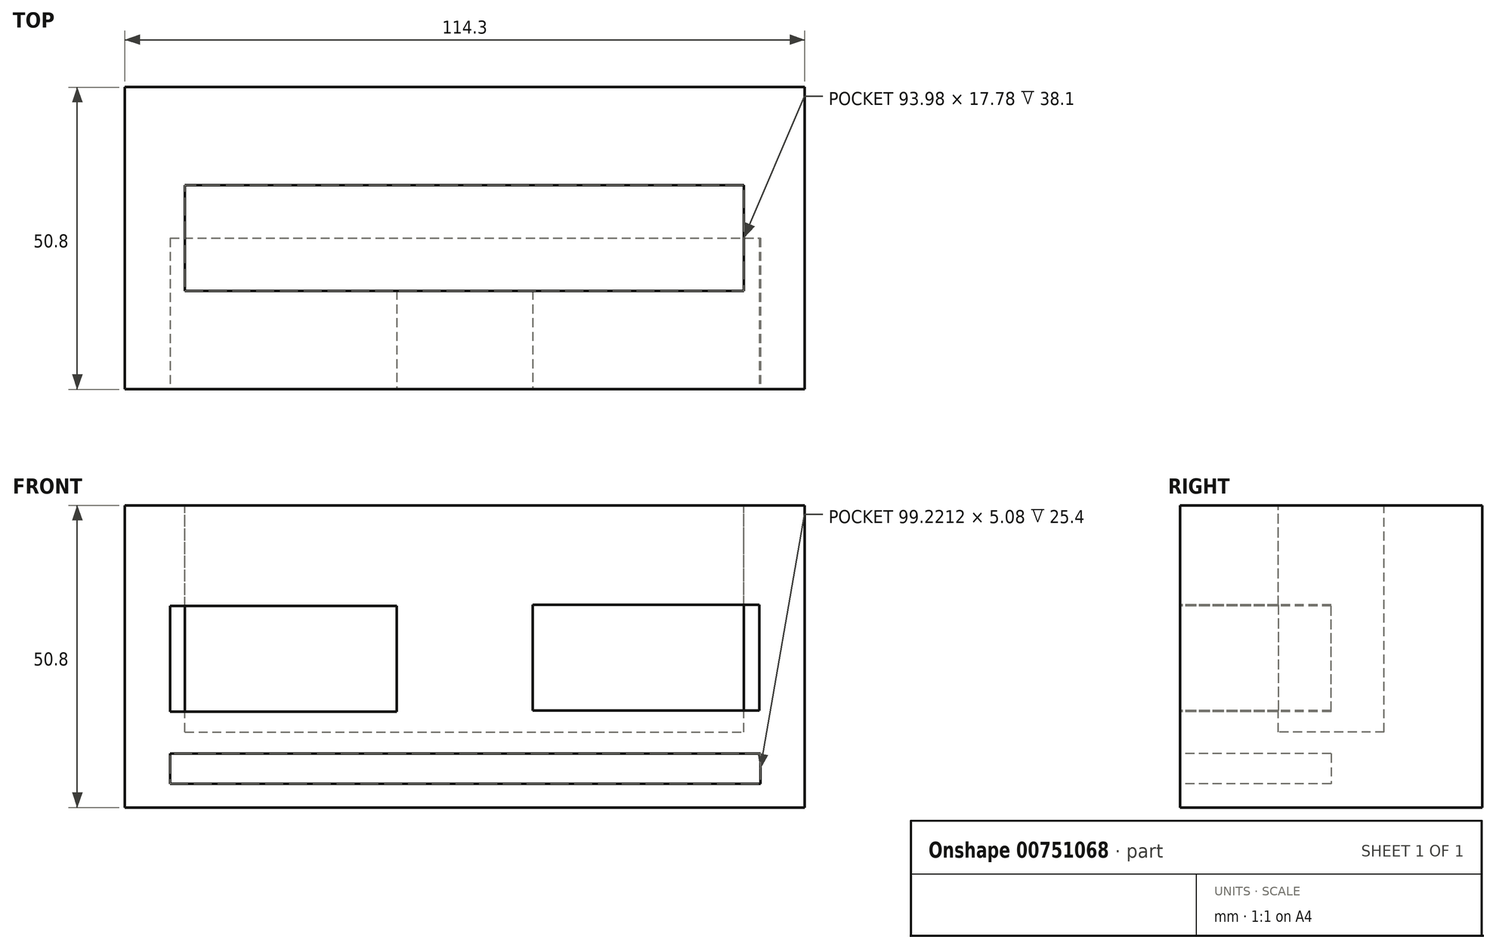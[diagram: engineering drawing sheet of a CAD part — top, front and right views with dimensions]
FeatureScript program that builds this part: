
annotation { "Feature Type Name" : "Feature", "Feature Type Description" : "" }
export const myFeature = defineFeature(function(context is Context, id is Id, definition is map)
    precondition{}
    {
        {
            var Q0;
            Q0=qCreatedBy(makeId("Top.planeOp"),FACE);
            var sketch = newSketch(context, id + "F0", { "sketchPlane" : qUnion([Q0])});
            skLineSegment(sketch, "E0.bottom", {"start": v(-58.02, 2.67) * mm, "end": v(56.28, 2.67) * mm});
            skLineSegment(sketch, "E0.top", {"start": v(-58.02, -48.13) * mm, "end": v(56.28, -48.13) * mm});
            skLineSegment(sketch, "E0.left", {"start": v(-58.02, 2.67) * mm, "end": v(-58.02, -48.13) * mm});
            skLineSegment(sketch, "E0.right", {"start": v(56.28, 2.67) * mm, "end": v(56.28, -48.13) * mm});
            skSolve(sketch);
        }
        {
            var Q0;
            Q0 = qSketchRegion(id + "F0", true);
            extrude(context, id + "F1", {"entities" : qUnion([Q0]), "depth" : 50.8 * mm, "offsetDistance" : 25.4 * mm});
        }
        {
            var Q0;
            Q0=makeQuery(id+"F1.opExtrude","CAP_FACE",FACE,{"disambiguationData":[OSD([sQuery(id+"F0.wireOp",EDGE,"E0.bottom"),sQuery(id+"F0.wireOp",EDGE,"E0.top"),sQuery(id+"F0.wireOp",EDGE,"E0.left"),sQuery(id+"F0.wireOp",EDGE,"E0.right")])],"isStart":false});
            var sketch = newSketch(context, id + "F2", { "sketchPlane" : qUnion([Q0])});
            skLineSegment(sketch, "E1", {"start": v(-58.02, -22.73) * mm, "end": v(56.28, -22.73) * mm, "construction": true});
            skLineSegment(sketch, "E2", {"start": v(-0.87, 2.67) * mm, "end": v(-0.87, -48.13) * mm, "construction": true});
            skLineSegment(sketch, "E3.bottom", {"start": v(-47.92, -13.8) * mm, "end": v(46.06, -13.8) * mm});
            skLineSegment(sketch, "E3.top", {"start": v(-47.92, -31.58) * mm, "end": v(46.06, -31.58) * mm});
            skLineSegment(sketch, "E3.left", {"start": v(-47.92, -13.8) * mm, "end": v(-47.92, -31.58) * mm});
            skLineSegment(sketch, "E3.right", {"start": v(46.06, -13.8) * mm, "end": v(46.06, -31.58) * mm});
            skLineSegment(sketch, "E4", {"start": v(-47.92, -22.69) * mm, "end": v(46.06, -22.69) * mm, "construction": true});
            skLineSegment(sketch, "E5", {"start": v(-0.93, -13.8) * mm, "end": v(-0.93, -31.58) * mm, "construction": true});
            skSolve(sketch);
        }
        {
            var Q0;
            Q0 = qSketchRegion(id + "F2", true);
            extrude(context, id + "F3", {"entities" : qUnion([Q0]), "operationType" : NewBodyOperationType.REMOVE, "oppositeDirection" : true, "depth" : 38.1 * mm, "offsetDistance" : 25.4 * mm});
        }
        {
            var Q0;
            Q0=makeQuery(id+"F1.opExtrude","SWEPT_FACE",FACE,{"disambiguationData":[OSD([sQuery(id+"F0.wireOp",EDGE,"E0.top")])]});
            var sketch = newSketch(context, id + "F4", { "sketchPlane" : qUnion([Q0])});
            skLineSegment(sketch, "E6", {"start": v(-58.02, 25.4) * mm, "end": v(56.28, 25.4) * mm, "construction": true});
            skLineSegment(sketch, "E7", {"start": v(0, 50.8) * mm, "end": v(0, 0) * mm, "construction": true});
            skLineSegment(sketch, "E8", {"start": v(-27.68, 0) * mm, "end": v(-27.68, 50.8) * mm, "construction": true});
            skLineSegment(sketch, "E9", {"start": v(-27.68, 33.9) * mm, "end": v(-27.68, 25.4) * mm, "construction": true});
            skLineSegment(sketch, "E10", {"start": v(-27.68, 25.4) * mm, "end": v(-27.68, 15.7) * mm, "construction": true});
            skLineSegment(sketch, "E11", {"start": v(-48.1, 25.4) * mm, "end": v(-12.54, 25.4) * mm, "construction": true});
            skLineSegment(sketch, "E12", {"start": v(-27.68, 50.8) * mm, "end": v(35.82, 50.8) * mm, "construction": true});
            skLineSegment(sketch, "E13", {"start": v(35.82, 50.8) * mm, "end": v(35.82, 0) * mm, "construction": true});
            skLineSegment(sketch, "E14.bottom", {"start": v(10.56, 34.09) * mm, "end": v(48.66, 34.09) * mm});
            skLineSegment(sketch, "E14.top", {"start": v(10.56, 16.3) * mm, "end": v(48.66, 16.3) * mm});
            skLineSegment(sketch, "E14.left", {"start": v(10.56, 34.09) * mm, "end": v(10.56, 16.3) * mm});
            skLineSegment(sketch, "E14.right", {"start": v(48.66, 34.09) * mm, "end": v(48.66, 16.3) * mm});
            skLineSegment(sketch, "E15", {"start": v(29.6, 34.09) * mm, "end": v(29.6, 16.3) * mm, "construction": true});
            skLineSegment(sketch, "E16", {"start": v(10.56, 25.2) * mm, "end": v(48.66, 25.2) * mm, "construction": true});
            skLineSegment(sketch, "E17.bottom", {"start": v(-50.4, 33.9) * mm, "end": v(-12.3, 33.9) * mm});
            skLineSegment(sketch, "E17.top", {"start": v(-50.4, 16.12) * mm, "end": v(-12.3, 16.12) * mm});
            skLineSegment(sketch, "E17.left", {"start": v(-50.4, 33.9) * mm, "end": v(-50.4, 16.12) * mm});
            skLineSegment(sketch, "E17.right", {"start": v(-12.3, 33.9) * mm, "end": v(-12.3, 16.12) * mm});
            skLineSegment(sketch, "E18", {"start": v(-31.35, 33.9) * mm, "end": v(-27.68, 16.12) * mm, "construction": true});
            skLineSegment(sketch, "E19", {"start": v(-50.4, 25.01) * mm, "end": v(-12.3, 25.01) * mm, "construction": true});
            skLineSegment(sketch, "E20", {"start": v(-50.4, 16.12) * mm, "end": v(-58.02, 16.12) * mm, "construction": true});
            skLineSegment(sketch, "E21", {"start": v(48.66, 16.3) * mm, "end": v(56.28, 16.3) * mm, "construction": true});
            skLineSegment(sketch, "E22.bottom", {"start": v(-50.4, 9.03) * mm, "end": v(48.82, 9.03) * mm});
            skLineSegment(sketch, "E22.top", {"start": v(-50.4, 3.95) * mm, "end": v(48.82, 3.95) * mm});
            skLineSegment(sketch, "E22.left", {"start": v(-50.4, 9.03) * mm, "end": v(-50.4, 3.95) * mm});
            skLineSegment(sketch, "E22.right", {"start": v(48.82, 9.03) * mm, "end": v(48.82, 3.95) * mm});
            skLineSegment(sketch, "E23", {"start": v(-50.4, 16.12) * mm, "end": v(-50.4, 9.03) * mm, "construction": true});
            skLineSegment(sketch, "E24", {"start": v(48.66, 16.3) * mm, "end": v(48.82, 9.03) * mm, "construction": true});
            skSolve(sketch);
        }
        {
            var Q0;
            Q0 = qSketchRegion(id + "F4", true);
            extrude(context, id + "F5", {"entities" : qUnion([Q0]), "operationType" : NewBodyOperationType.REMOVE, "oppositeDirection" : true, "depth" : 25.4 * mm, "offsetDistance" : 25.4 * mm});
        }
        {
            var Q0;
            Q0 = qSketchRegion(id + "F4", true);
            extrude(context, id + "F6", {"entities" : qUnion([Q0]), "operationType" : NewBodyOperationType.REMOVE, "oppositeDirection" : true, "depth" : 25.4 * mm, "offsetDistance" : 25.4 * mm});
        }
    });
